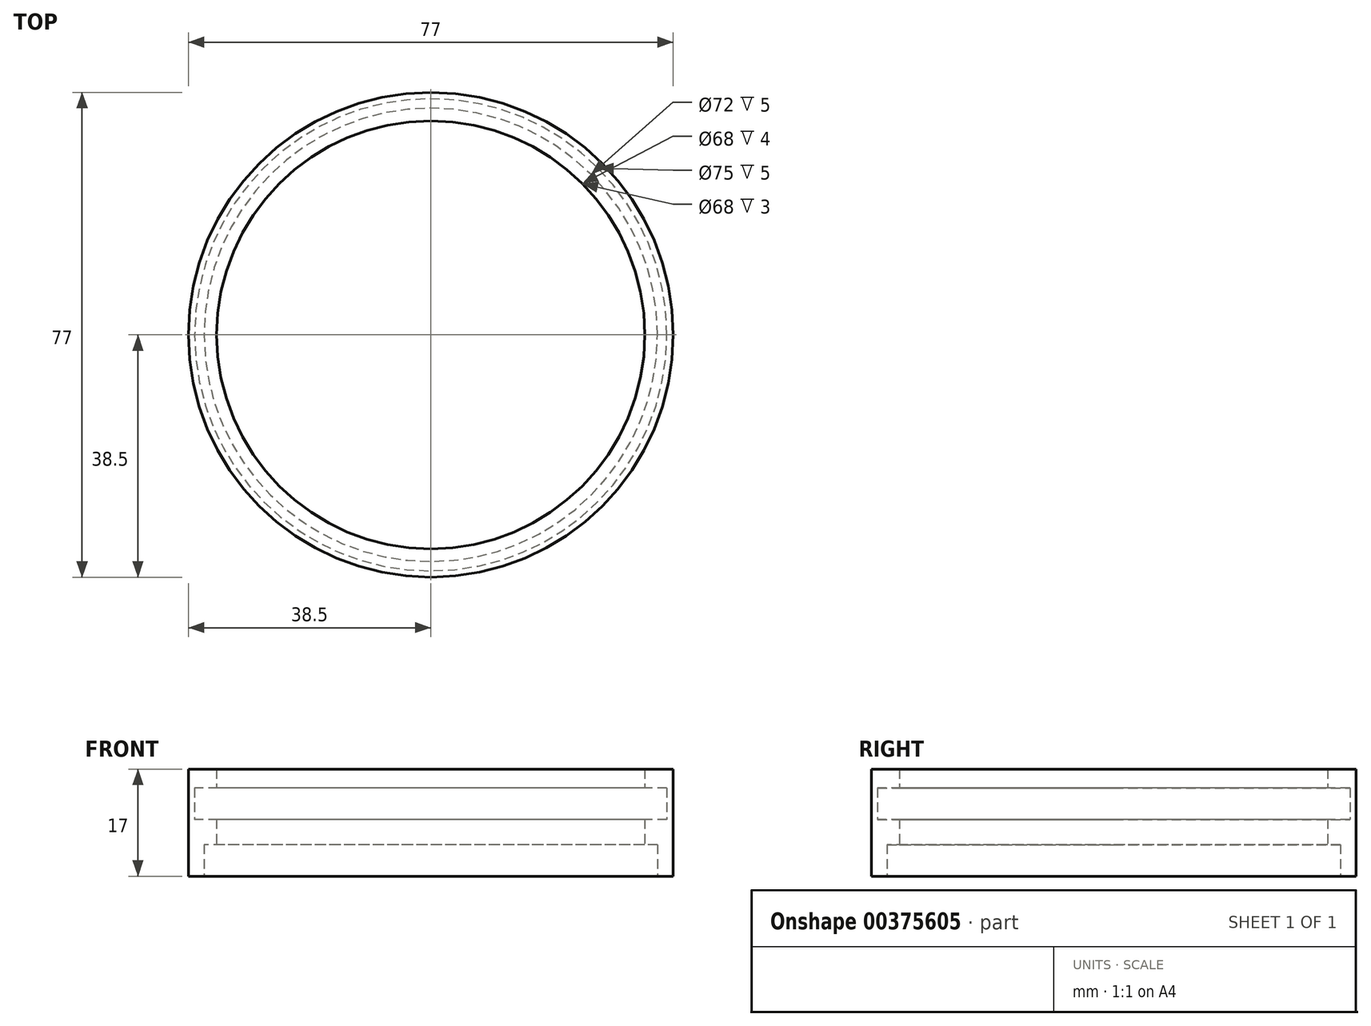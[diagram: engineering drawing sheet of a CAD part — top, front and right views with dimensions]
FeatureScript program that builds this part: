
annotation { "Feature Type Name" : "Feature", "Feature Type Description" : "" }
export const myFeature = defineFeature(function(context is Context, id is Id, definition is map)
    precondition{}
    {
        {
            var Q0;
            Q0=qCreatedBy(makeId("Top.planeOp"),FACE);
            var sketch = newSketch(context, id + "F0", { "sketchPlane" : qUnion([Q0])});
            skCircle(sketch, "E0", {"center": v(0, 0) * mm, "radius": 38.5 * mm});
            skCircle(sketch, "E1", {"center": v(0, 0) * mm, "radius": 36 * mm});
            skSolve(sketch);
        }
        {
            var Q0;
            Q0=makeQuery(id+"F0.imprint","IMPRINT",FACE,{"disambiguationData":[TD([[makeQuery(id+"F0.imprint","IMPRINT",EDGE,{"derivedFrom":sQuery(id+"F0.wireOp",EDGE,"E0")}),1.0]])]});
            extrude(context, id + "F1", {"entities" : qUnion([Q0]), "depth" : 5 * mm});
        }
        {
            var Q0;
            Q0=makeQuery(id+"F1.opExtrude","CAP_FACE",FACE,{"disambiguationData":[OSD([sQuery(id+"F0.wireOp",EDGE,"E0"),sQuery(id+"F0.wireOp",EDGE,"E1")])],"isStart":false});
            var sketch = newSketch(context, id + "F2", { "sketchPlane" : qUnion([Q0])});
            skCircle(sketch, "E2", {"center": v(0, 0) * mm, "radius": 36 * mm});
            skPoint(sketch, "E2.first.point", {"position": v(-14.63, -32.9) * mm});
            skPoint(sketch, "E2.second.point", {"position": v(22.51, 28.1) * mm});
            skPoint(sketch, "E2.third.point", {"position": v(-18.28, 31.01) * mm});
            skCircle(sketch, "E3", {"center": v(0, 0) * mm, "radius": 34 * mm});
            skCircle(sketch, "E4", {"center": v(0, 0) * mm, "radius": 38.5 * mm});
            skSolve(sketch);
        }
        {
            var Q0;
            Q0 = qSketchRegion(id + "F2", true);
            var Q1;
            Q1=makeQuery(id+"F2.imprint","IMPRINT",FACE,{"disambiguationData":[TD([[makeQuery(id+"F2.imprint","IMPRINT",EDGE,{"derivedFrom":sQuery(id+"F2.wireOp",EDGE,"E2")}),1.0]])]});
            extrude(context, id + "F3", {"entities" : qUnion([Q0, Q1]), "operationType" : NewBodyOperationType.ADD, "depth" : 4 * mm});
        }
        {
            var Q0;
            Q0=makeQuery(id+"F3.opExtrude","CAP_FACE",FACE,{"disambiguationData":[OSD([sQuery(id+"F2.wireOp",EDGE,"E3"),sQuery(id+"F2.wireOp",EDGE,"E4")])],"isStart":false});
            var sketch = newSketch(context, id + "F4", { "sketchPlane" : qUnion([Q0])});
            skCircle(sketch, "E5", {"center": v(0, 0) * mm, "radius": 38.5 * mm});
            skPoint(sketch, "E5.first.point", {"position": v(-26.86, -27.58) * mm});
            skPoint(sketch, "E5.second.point", {"position": v(2.3, 38.43) * mm});
            skPoint(sketch, "E5.third.point", {"position": v(35.66, 14.52) * mm});
            skCircle(sketch, "E6", {"center": v(0, 0) * mm, "radius": 37.5 * mm});
            skSolve(sketch);
        }
        {
            var Q0;
            Q0 = qSketchRegion(id + "F4", true);
            extrude(context, id + "F5", {"entities" : qUnion([Q0]), "operationType" : NewBodyOperationType.ADD, "depth" : 5 * mm});
        }
        {
            var Q0;
            Q0=makeQuery(id+"F5.opExtrude","CAP_FACE",FACE,{"disambiguationData":[OSD([sQuery(id+"F4.wireOp",EDGE,"E5"),sQuery(id+"F4.wireOp",EDGE,"E6")])],"isStart":false});
            var sketch = newSketch(context, id + "F6", { "sketchPlane" : qUnion([Q0])});
            skCircle(sketch, "E7", {"center": v(0, 0) * mm, "radius": 38.5 * mm});
            skPoint(sketch, "E7.first.point", {"position": v(-35.4, 15.13) * mm});
            skPoint(sketch, "E7.second.point", {"position": v(36.8, -11.34) * mm});
            skPoint(sketch, "E7.third.point", {"position": v(11.11, 36.86) * mm});
            skCircle(sketch, "E8", {"center": v(0, 0) * mm, "radius": 34 * mm});
            skSolve(sketch);
        }
        {
            var Q0;
            Q0 = qSketchRegion(id + "F6", true);
            extrude(context, id + "F7", {"entities" : qUnion([Q0]), "operationType" : NewBodyOperationType.ADD, "depth" : 3 * mm});
        }
    });
